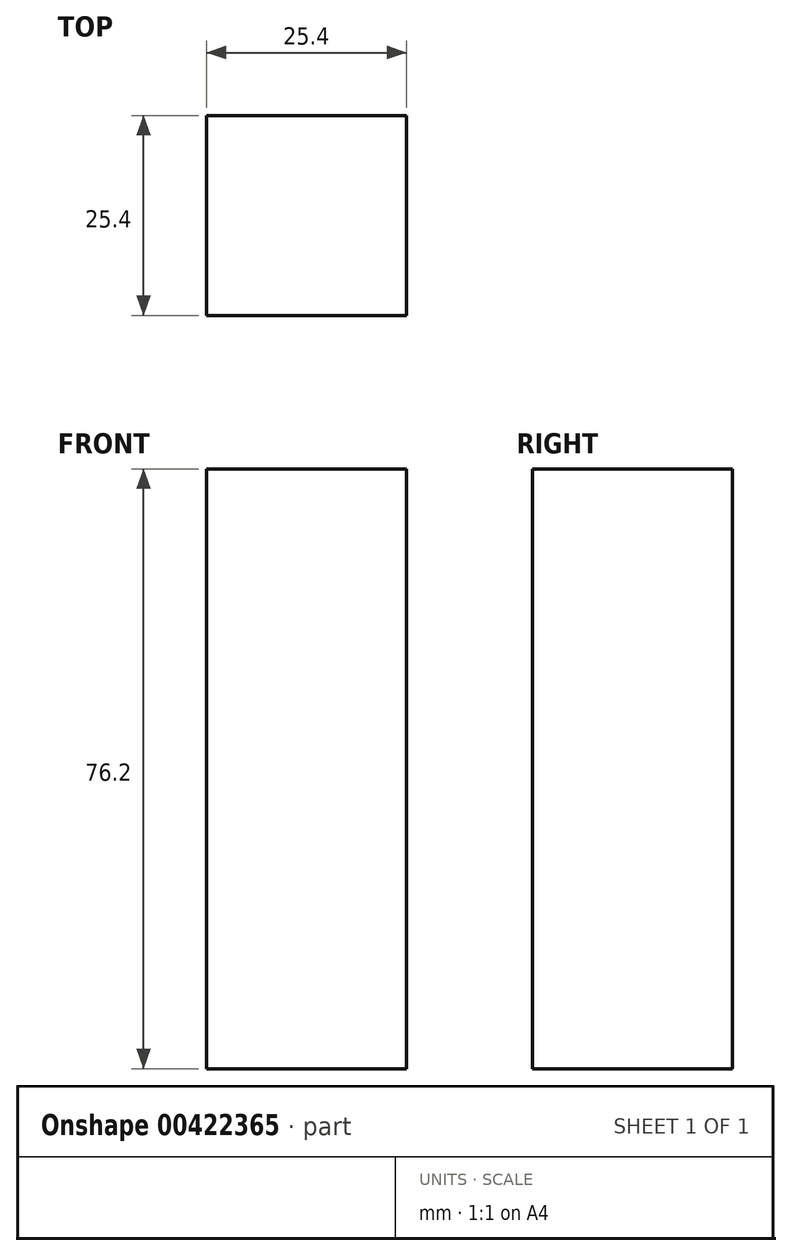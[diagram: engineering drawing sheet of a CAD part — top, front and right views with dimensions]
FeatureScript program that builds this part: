
annotation { "Feature Type Name" : "Feature", "Feature Type Description" : "" }
export const myFeature = defineFeature(function(context is Context, id is Id, definition is map)
    precondition{}
    {
        {
            var Q0;
            Q0=qCreatedBy(makeId("Front.planeOp"),FACE);
            var sketch = newSketch(context, id + "F0", { "sketchPlane" : qUnion([Q0])});
            skLineSegment(sketch, "E0.bottom", {"start": v(0, -25.78) * mm, "end": v(-25.4, -25.78) * mm});
            skLineSegment(sketch, "E0.top", {"start": v(0, 50.42) * mm, "end": v(-25.4, 50.42) * mm});
            skLineSegment(sketch, "E0.left", {"start": v(0, -25.78) * mm, "end": v(0, 50.42) * mm});
            skLineSegment(sketch, "E0.right", {"start": v(-25.4, -25.78) * mm, "end": v(-25.4, 50.42) * mm});
            skSolve(sketch);
        }
        {
            var Q0;
            Q0 = qSketchRegion(id + "F0", true);
            extrude(context, id + "F1", {"entities" : qUnion([Q0]), "depth" : 25.4 * mm});
        }
    });
